# Revit family: Steel-RHS+SHS Section-Steel & Tube-C350L0 A
name_source: partatom
category: Structural Framing
revit_build: Autodesk Revit 2018 (Build: 20170927_1515(x64)
units: mm (PartAtom-declared; Revit-internal decimal feet)

## family parameters
Always export as geometry = No
Always vertical = Yes
Cut with Voids When Loaded = No
Material for Model Behavior = Steel
OmniClass Number = 23.25.30.11.14.14
OmniClass Title = Beams
Section Shape = Rectangular HSS
Shared = No
Show family pre-cut in plan views = Yes
Structural Framing Length Roundoff = 0 mm

## types (1)
- 150x50x6.0 RHS
    Assembly Code = B1020230
    CBICode = 3421
    CBIDescription = Light steel framing
    Centroid Horizontal = 25.0 mm
    Centroid Vertical = 75.0 mm
    Description = Steel & Tube supplies a full range of hot rolled seismic and non seismic universal beams, columns, plate and channels. For more information please refer to the Design with Steel product catalogue on our website.
    Design Instruction = Design information should be cross referenced with the Steel & Tube Design with Steel Design Guide and NZS 3404: Part1: 2009
    Design Standard = NZS 3404: Part 1: 2009 including reference to the NZBC
    Elastic Modulus strong axis = 91200.0 mm³
    Elastic Modulus weak axis = 40900.0 mm³
    Form Factor = 0
    Height = 150.0 mm
    Inner Fillet = 11.3 mm
    Manufactured Standard = AS/NZS 1163: 2016
    Manufacturer = Steel & Tube
    ManufacturerName = Steel & Tube
    ManufacturerURL = http://www.steelandtube.co.nz
    MassPerUnitLength_ANZRS = 16.70 kg/m
    Model = RHS150x50x6.0
    ModifiedIssue_ANZRS = 20160330 $
    Moment of Inertia strong axis = 5060000.00 mm4
    Moment of Inertia weak axis = 860000.00 mm4
    Nominal Weight = 16.70 kgf/m
    Outer Fillet = 18.8 mm
    Perimeter = 0.37 m²/m
    Plastic Modulus strong axis = 67500.0 mm³
    Plastic Modulus weak axis = 34400.0 mm³
    Principal Axes Angle = 0.00°
    Section Area = 2130.0 mm²
    SectionAreaGross_ANZRS = 2130.0 mm²
    SectionAreaNet_ANZRS = 2130.0 mm²
    Shear Area strong axis = 2130.0 mm²
    Shear Area weak axis = 2130.0 mm²
    Tensile Strength = 0.0 MPa
    Torsional Modulus = 64300.0 mm³
    Torsional Moment of Inertia = 2630000.00 mm4
    URL = http://www.steelandtube.co.nz
    Uniclass2015Code = Pr_20_76_51_12
    Uniclass2015Title = Carbon steel beams, columns, channels and tees
    Uniclass2015Version = 2015
    Wall Design Thickness = 7.5 mm
    Wall Nominal Thickness = 6.0 mm
    Warping Constant = 0.0 mm6
    Width = 50.0 mm
    X-Zex = 0.0 mm³
    Y-Zey = 0.0 mm³
    Yield Stress = 0.0 MPa

## geometry (parser evidence)
native form markers: Sweep x5
no freeform markers — native parametric forms only
